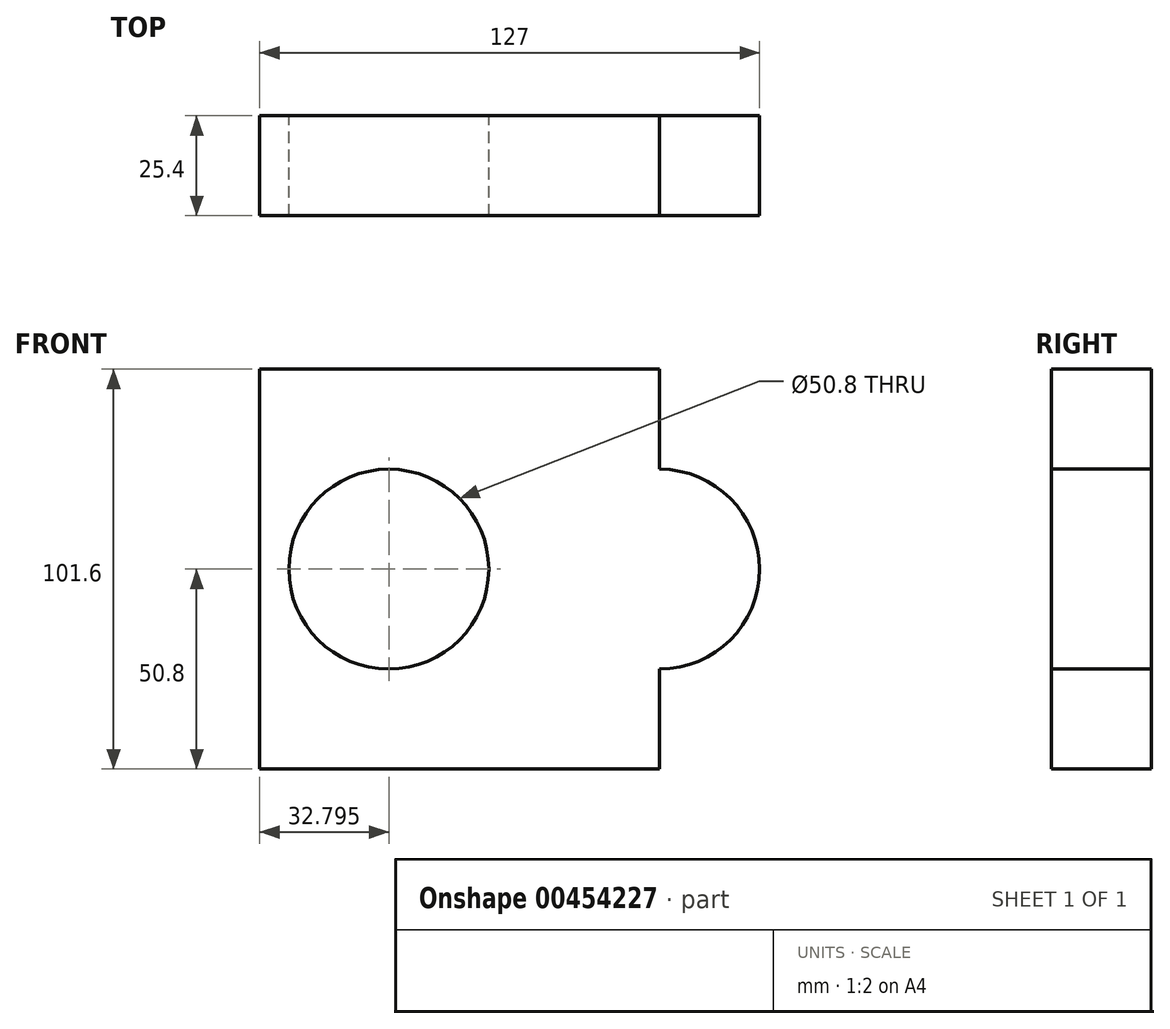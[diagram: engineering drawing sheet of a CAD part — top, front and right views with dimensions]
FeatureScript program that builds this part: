
annotation { "Feature Type Name" : "Feature", "Feature Type Description" : "" }
export const myFeature = defineFeature(function(context is Context, id is Id, definition is map)
    precondition{}
    {
        {
            var Q0;
            Q0=qCreatedBy(makeId("Front.planeOp"),FACE);
            var sketch = newSketch(context, id + "F0", { "sketchPlane" : qUnion([Q0])});
            skLineSegment(sketch, "E0.bottom", {"start": v(50.8, -50.8) * mm, "end": v(-50.8, -50.8) * mm});
            skLineSegment(sketch, "E0.top", {"start": v(50.8, 50.8) * mm, "end": v(-50.8, 50.8) * mm});
            skLineSegment(sketch, "E0.left", {"start": v(50.8, -50.8) * mm, "end": v(50.8, 50.8) * mm});
            skLineSegment(sketch, "E0.right", {"start": v(-50.8, -50.8) * mm, "end": v(-50.8, 50.8) * mm});
            skPoint(sketch, "E0.middle", {"position": v(0, 0) * mm});
            skPoint(sketch, "E1", {"position": v(-18, 0) * mm});
            skPoint(sketch, "E2", {"position": v(50.8, 0) * mm});
            skCircle(sketch, "E3", {"center": v(-18, 0) * mm, "radius": 25.4 * mm});
            skCircle(sketch, "E4", {"center": v(50.8, 0) * mm, "radius": 25.4 * mm});
            skSolve(sketch);
        }
        {
            var Q0;
            Q0 = qSketchRegion(id + "F0", true);
            extrude(context, id + "F1", {"entities" : qUnion([Q0]), "depth" : 25.4 * mm});
        }
    });
